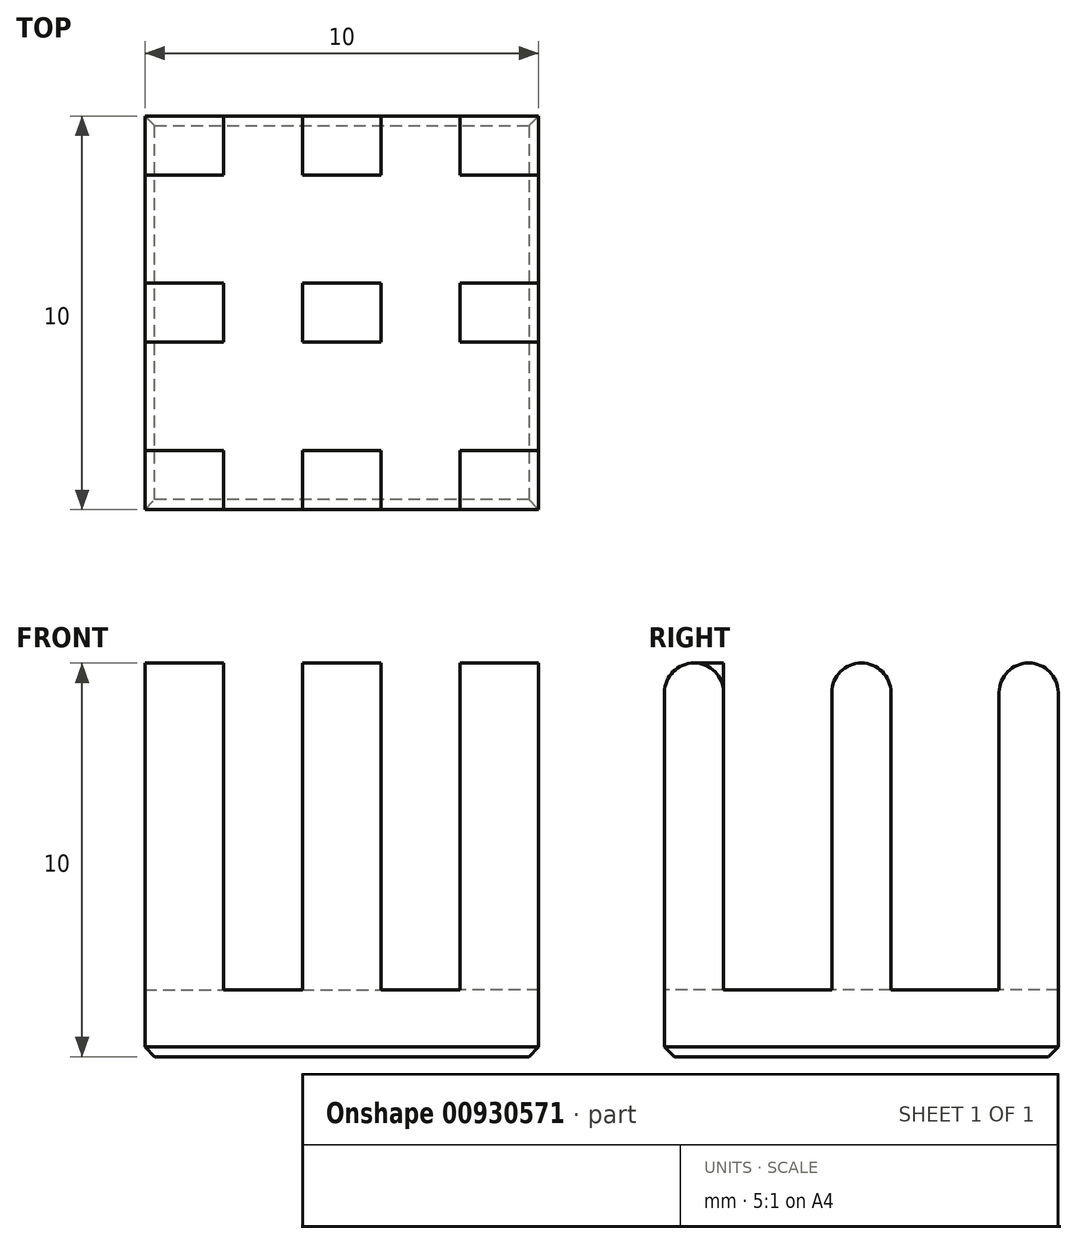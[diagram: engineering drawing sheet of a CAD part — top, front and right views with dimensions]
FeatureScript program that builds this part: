
annotation { "Feature Type Name" : "Feature", "Feature Type Description" : "" }
export const myFeature = defineFeature(function(context is Context, id is Id, definition is map)
    precondition{}
    {
        {
            var Q0;
            Q0=qCreatedBy(makeId("Top.planeOp"),FACE);
            var sketch = newSketch(context, id + "F0", { "sketchPlane" : qUnion([Q0])});
            skLineSegment(sketch, "E0.bottom", {"start": v(0, 0) * mm, "end": v(10, 0) * mm});
            skLineSegment(sketch, "E0.top", {"start": v(0, 10) * mm, "end": v(10, 10) * mm});
            skLineSegment(sketch, "E0.left", {"start": v(0, 0) * mm, "end": v(0, 10) * mm});
            skLineSegment(sketch, "E0.right", {"start": v(10, 0) * mm, "end": v(10, 10) * mm});
            skSolve(sketch);
        }
        {
            var Q0;
            Q0=qSketchRegion(id+"F0",true);
            extrude(context, id + "F1", {"entities" : qUnion([Q0]), "depth" : 1.7 * mm});
        }
        {
            var Q0;
            Q0=makeQuery(id+"F1.opExtrude","CAP_EDGE",EDGE,{"disambiguationData":[OSD([sQuery(id+"F0.wireOp",EDGE,"E0.bottom")])],"isStart":true});
            var Q1;
            Q1=makeQuery(id+"F1.opExtrude","CAP_EDGE",EDGE,{"disambiguationData":[OSD([sQuery(id+"F0.wireOp",EDGE,"E0.left")])],"isStart":true});
            var Q2;
            Q2=makeQuery(id+"F1.opExtrude","CAP_EDGE",EDGE,{"disambiguationData":[OSD([sQuery(id+"F0.wireOp",EDGE,"E0.right")])],"isStart":true});
            var Q3;
            Q3=makeQuery(id+"F1.opExtrude","CAP_EDGE",EDGE,{"disambiguationData":[OSD([sQuery(id+"F0.wireOp",EDGE,"E0.top")])],"isStart":true});
            chamfer(context, id + "F2", {"entities" : qUnion([Q0, Q1, Q2, Q3]), "width" : 0.25 * mm, "tangentPropagation" : true});
        }
        {
            var Q0;
            Q0=makeQuery(id+"F1.opExtrude","CAP_FACE",FACE,{"disambiguationData":[OSD([sQuery(id+"F0.wireOp",EDGE,"E0.bottom"),sQuery(id+"F0.wireOp",EDGE,"E0.top"),sQuery(id+"F0.wireOp",EDGE,"E0.left"),sQuery(id+"F0.wireOp",EDGE,"E0.right")])],"isStart":false});
            var sketch = newSketch(context, id + "F3", { "sketchPlane" : qUnion([Q0])});
            skLineSegment(sketch, "E1.bottom", {"start": v(0, 10) * mm, "end": v(2, 10) * mm});
            skLineSegment(sketch, "E1.top", {"start": v(0, 8.5) * mm, "end": v(2, 8.5) * mm});
            skLineSegment(sketch, "E1.left", {"start": v(0, 10) * mm, "end": v(0, 8.5) * mm});
            skLineSegment(sketch, "E1.right", {"start": v(2, 10) * mm, "end": v(2, 8.5) * mm});
            skLineSegment(sketch, "E2.bottom", {"start": v(10, 10) * mm, "end": v(8, 10) * mm});
            skLineSegment(sketch, "E2.top", {"start": v(10, 8.5) * mm, "end": v(8, 8.5) * mm});
            skLineSegment(sketch, "E2.left", {"start": v(10, 10) * mm, "end": v(10, 8.5) * mm});
            skLineSegment(sketch, "E2.right", {"start": v(8, 10) * mm, "end": v(8, 8.5) * mm});
            skLineSegment(sketch, "E3.bottom", {"start": v(0, 0) * mm, "end": v(2, 0) * mm});
            skLineSegment(sketch, "E3.top", {"start": v(0, 1.5) * mm, "end": v(2, 1.5) * mm});
            skLineSegment(sketch, "E3.left", {"start": v(0, 0) * mm, "end": v(0, 1.5) * mm});
            skLineSegment(sketch, "E3.right", {"start": v(2, 0) * mm, "end": v(2, 1.5) * mm});
            skLineSegment(sketch, "E4.bottom", {"start": v(10, 0) * mm, "end": v(8, 0) * mm});
            skLineSegment(sketch, "E4.top", {"start": v(10, 1.5) * mm, "end": v(8, 1.5) * mm});
            skLineSegment(sketch, "E4.left", {"start": v(10, 0) * mm, "end": v(10, 1.5) * mm});
            skLineSegment(sketch, "E4.right", {"start": v(8, 0) * mm, "end": v(8, 1.5) * mm});
            skLineSegment(sketch, "E5.bottom", {"start": v(0, 5.75) * mm, "end": v(2, 5.75) * mm});
            skLineSegment(sketch, "E5.top", {"start": v(0, 4.25) * mm, "end": v(2, 4.25) * mm});
            skLineSegment(sketch, "E5.left", {"start": v(0, 5.75) * mm, "end": v(0, 4.25) * mm});
            skLineSegment(sketch, "E5.right", {"start": v(2, 5.75) * mm, "end": v(2, 4.25) * mm});
            skLineSegment(sketch, "E6.bottom", {"start": v(4, 10) * mm, "end": v(6, 10) * mm});
            skLineSegment(sketch, "E6.top", {"start": v(4, 8.5) * mm, "end": v(6, 8.5) * mm});
            skLineSegment(sketch, "E6.left", {"start": v(4, 10) * mm, "end": v(4, 8.5) * mm});
            skLineSegment(sketch, "E6.right", {"start": v(6, 10) * mm, "end": v(6, 8.5) * mm});
            skLineSegment(sketch, "E7.bottom", {"start": v(10, 5.75) * mm, "end": v(8, 5.75) * mm});
            skLineSegment(sketch, "E7.top", {"start": v(10, 4.25) * mm, "end": v(8, 4.25) * mm});
            skLineSegment(sketch, "E7.left", {"start": v(10, 5.75) * mm, "end": v(10, 4.25) * mm});
            skLineSegment(sketch, "E7.right", {"start": v(8, 5.75) * mm, "end": v(8, 4.25) * mm});
            skLineSegment(sketch, "E8.bottom", {"start": v(4, 5.75) * mm, "end": v(6, 5.75) * mm});
            skLineSegment(sketch, "E8.top", {"start": v(4, 4.25) * mm, "end": v(6, 4.25) * mm});
            skLineSegment(sketch, "E8.left", {"start": v(4, 5.75) * mm, "end": v(4, 4.25) * mm});
            skLineSegment(sketch, "E8.right", {"start": v(6, 5.75) * mm, "end": v(6, 4.25) * mm});
            skLineSegment(sketch, "E9.bottom", {"start": v(4, 1.5) * mm, "end": v(6, 1.5) * mm});
            skLineSegment(sketch, "E9.top", {"start": v(4, 0) * mm, "end": v(6, 0) * mm});
            skLineSegment(sketch, "E9.left", {"start": v(4, 1.5) * mm, "end": v(4, 0) * mm});
            skLineSegment(sketch, "E9.right", {"start": v(6, 1.5) * mm, "end": v(6, 0) * mm});
            skSolve(sketch);
        }
        {
            var Q0;
            Q0=qSketchRegion(id+"F3",true);
            extrude(context, id + "F4", {"entities" : qUnion([Q0]), "operationType" : NewBodyOperationType.ADD, "depth" : 8.3 * mm});
        }
        {
            var Q0;
            Q0=makeQuery(id+"F4.opExtrude","CAP_EDGE",EDGE,{"disambiguationData":[OSD([sQuery(id+"F3.wireOp",EDGE,"E3.bottom")])],"isStart":false});
            var Q1;
            Q1=makeQuery(id+"F4.opExtrude","CAP_EDGE",EDGE,{"disambiguationData":[OSD([sQuery(id+"F3.wireOp",EDGE,"E3.top")])],"isStart":false});
            var Q2;
            Q2=makeQuery(id+"F4.opExtrude","CAP_EDGE",EDGE,{"disambiguationData":[OSD([sQuery(id+"F3.wireOp",EDGE,"E9.top")])],"isStart":false});
            var Q3;
            Q3=makeQuery(id+"F4.opExtrude","CAP_EDGE",EDGE,{"disambiguationData":[OSD([sQuery(id+"F3.wireOp",EDGE,"E4.bottom")])],"isStart":false});
            var Q4;
            Q4=makeQuery(id+"F4.opExtrude","CAP_EDGE",EDGE,{"disambiguationData":[OSD([sQuery(id+"F3.wireOp",EDGE,"E4.top")])],"isStart":false});
            var Q5;
            Q5=makeQuery(id+"F4.opExtrude","CAP_EDGE",EDGE,{"disambiguationData":[OSD([sQuery(id+"F3.wireOp",EDGE,"E7.top")])],"isStart":false});
            var Q6;
            Q6=makeQuery(id+"F4.opExtrude","CAP_EDGE",EDGE,{"disambiguationData":[OSD([sQuery(id+"F3.wireOp",EDGE,"E7.bottom")])],"isStart":false});
            var Q7;
            Q7=makeQuery(id+"F4.opExtrude","CAP_EDGE",EDGE,{"disambiguationData":[OSD([sQuery(id+"F3.wireOp",EDGE,"E8.top")])],"isStart":false});
            var Q8;
            Q8=makeQuery(id+"F4.opExtrude","CAP_EDGE",EDGE,{"disambiguationData":[OSD([sQuery(id+"F3.wireOp",EDGE,"E8.bottom")])],"isStart":false});
            var Q9;
            Q9=makeQuery(id+"F4.opExtrude","CAP_EDGE",EDGE,{"disambiguationData":[OSD([sQuery(id+"F3.wireOp",EDGE,"E5.top")])],"isStart":false});
            var Q10;
            Q10=makeQuery(id+"F4.opExtrude","CAP_EDGE",EDGE,{"disambiguationData":[OSD([sQuery(id+"F3.wireOp",EDGE,"E5.bottom")])],"isStart":false});
            var Q11;
            Q11=makeQuery(id+"F4.opExtrude","CAP_EDGE",EDGE,{"disambiguationData":[OSD([sQuery(id+"F3.wireOp",EDGE,"E1.top")])],"isStart":false});
            var Q12;
            Q12=makeQuery(id+"F4.opExtrude","CAP_EDGE",EDGE,{"disambiguationData":[OSD([sQuery(id+"F3.wireOp",EDGE,"E1.bottom")])],"isStart":false});
            var Q13;
            Q13=makeQuery(id+"F4.opExtrude","CAP_EDGE",EDGE,{"disambiguationData":[OSD([sQuery(id+"F3.wireOp",EDGE,"E6.top")])],"isStart":false});
            var Q14;
            Q14=makeQuery(id+"F4.opExtrude","CAP_EDGE",EDGE,{"disambiguationData":[OSD([sQuery(id+"F3.wireOp",EDGE,"E6.bottom")])],"isStart":false});
            var Q15;
            Q15=makeQuery(id+"F4.opExtrude","CAP_EDGE",EDGE,{"disambiguationData":[OSD([sQuery(id+"F3.wireOp",EDGE,"E2.top")])],"isStart":false});
            var Q16;
            Q16=makeQuery(id+"F4.opExtrude","CAP_EDGE",EDGE,{"disambiguationData":[OSD([sQuery(id+"F3.wireOp",EDGE,"E2.bottom")])],"isStart":false});
            fillet(context, id + "F5", {"entities" : qUnion([Q0, Q1, Q2, Q3, Q4, Q5, Q6, Q7, Q8, Q9, Q10, Q11, Q12, Q13, Q14, Q15, Q16]), "radius" : 0.75 * mm, "tangentPropagation" : true, "allowEdgeOverflow" : false});
        }
    });
